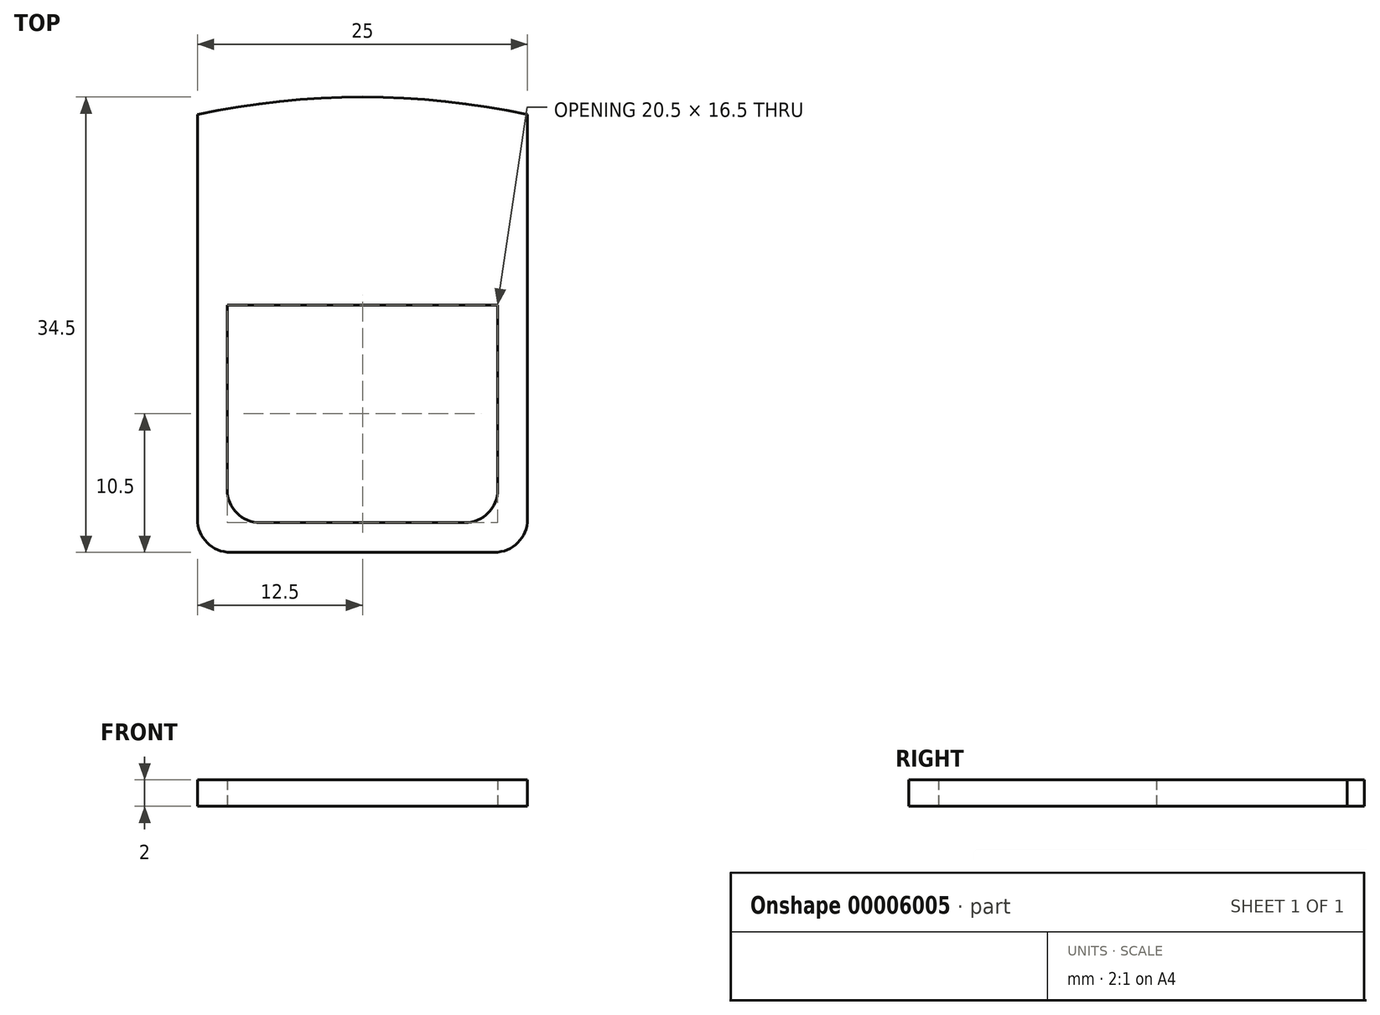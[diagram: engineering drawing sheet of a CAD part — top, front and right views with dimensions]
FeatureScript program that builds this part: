
annotation { "Feature Type Name" : "Feature", "Feature Type Description" : "" }
export const myFeature = defineFeature(function(context is Context, id is Id, definition is map)
    precondition{}
    {
        {
            var Q0;
            Q0=qCreatedBy(makeId("Top.planeOp"),FACE);
            var sketch = newSketch(context, id + "F0", { "sketchPlane" : qUnion([Q0])});
            skLineSegment(sketch, "E0.rect.bottom", {"start": v(12.5, -12.5) * mm, "end": v(-12.5, -12.5) * mm});
            skLineSegment(sketch, "E0.rect.top", {"start": v(12.5, 12.5) * mm, "end": v(-12.5, 12.5) * mm});
            skLineSegment(sketch, "E0.rect.left", {"start": v(12.5, -12.5) * mm, "end": v(12.5, 12.5) * mm});
            skLineSegment(sketch, "E0.rect.right", {"start": v(-12.5, -12.5) * mm, "end": v(-12.5, 12.5) * mm});
            skPoint(sketch, "E0.rect.middle", {"position": v(0, 0) * mm});
            skLineSegment(sketch, "E1.bottom", {"start": v(-10.25, -10.25) * mm, "end": v(10.25, -10.25) * mm});
            skLineSegment(sketch, "E1.top", {"start": v(-10.25, 6.25) * mm, "end": v(10.25, 6.25) * mm});
            skLineSegment(sketch, "E1.left", {"start": v(-10.25, -10.25) * mm, "end": v(-10.25, 6.25) * mm});
            skLineSegment(sketch, "E1.right", {"start": v(10.25, -10.25) * mm, "end": v(10.25, 6.25) * mm});
            skSolve(sketch);
        }
        {
            var Q0;
            Q0 = qSketchRegion(id + "F0", true);
            extrude(context, id + "F1", {"entities" : qUnion([Q0]), "depth" : 2 * mm});
        }
        {
            var Q0;
            Q0=makeQuery(id+"F1.opExtrude","SWEPT_EDGE",EDGE,{"disambiguationData":[OSD([sQuery(id+"F0.wireOp",EDGE,"E1.bottom"),sQuery(id+"F0.wireOp",EDGE,"E1.left")])]});
            var Q1;
            Q1=makeQuery(id+"F1.opExtrude","SWEPT_EDGE",EDGE,{"disambiguationData":[OSD([sQuery(id+"F0.wireOp",EDGE,"E1.bottom"),sQuery(id+"F0.wireOp",EDGE,"E1.right")])]});
            var Q2;
            Q2=makeQuery(id+"F1.opExtrude","SWEPT_EDGE",EDGE,{"disambiguationData":[OSD([sQuery(id+"F0.wireOp",EDGE,"E0.rect.bottom"),sQuery(id+"F0.wireOp",EDGE,"E0.rect.right")])]});
            var Q3;
            Q3=makeQuery(id+"F1.opExtrude","SWEPT_EDGE",EDGE,{"disambiguationData":[OSD([sQuery(id+"F0.wireOp",EDGE,"E0.rect.bottom"),sQuery(id+"F0.wireOp",EDGE,"E0.rect.left")])]});
            fillet(context, id + "F2", {"entities" : qUnion([Q0, Q1, Q2, Q3]), "radius" : 2.5 * mm, "tangentPropagation" : true, "allowEdgeOverflow" : false});
        }
        {
            var Q0;
            Q0=makeQuery(id+"F1.opExtrude","CAP_FACE",FACE,{"disambiguationData":[OSD([sQuery(id+"F0.wireOp",EDGE,"E0.rect.bottom"),sQuery(id+"F0.wireOp",EDGE,"E0.rect.top"),sQuery(id+"F0.wireOp",EDGE,"E0.rect.left"),sQuery(id+"F0.wireOp",EDGE,"E0.rect.right"),sQuery(id+"F0.wireOp",EDGE,"E1.bottom"),sQuery(id+"F0.wireOp",EDGE,"E1.top"),sQuery(id+"F0.wireOp",EDGE,"E1.left"),sQuery(id+"F0.wireOp",EDGE,"E1.right")])],"isStart":false});
            var sketch = newSketch(context, id + "F3", { "sketchPlane" : qUnion([Q0])});
            skLineSegment(sketch, "E2", {"start": v(-12.5, 12.5) * mm, "end": v(-12.5, 20.68) * mm});
            skLineSegment(sketch, "E3", {"start": v(12.5, 12.5) * mm, "end": v(12.5, 20.68) * mm});
            skArc(sketch, "E4", {"start": v(12.5, 20.68) * mm, "mid": v(0, 22) * mm, "end": v(-12.5, 20.68) * mm});
            skLineSegment(sketch, "E5", {"start": v(-12.5, 12.5) * mm, "end": v(12.5, 12.5) * mm});
            skSolve(sketch);
        }
        {
            var Q0;
            Q0 = qSketchRegion(id + "F3", true);
            extrude(context, id + "F4", {"entities" : qUnion([Q0]), "operationType" : NewBodyOperationType.ADD, "oppositeDirection" : true, "depth" : 2 * mm});
        }
    });
